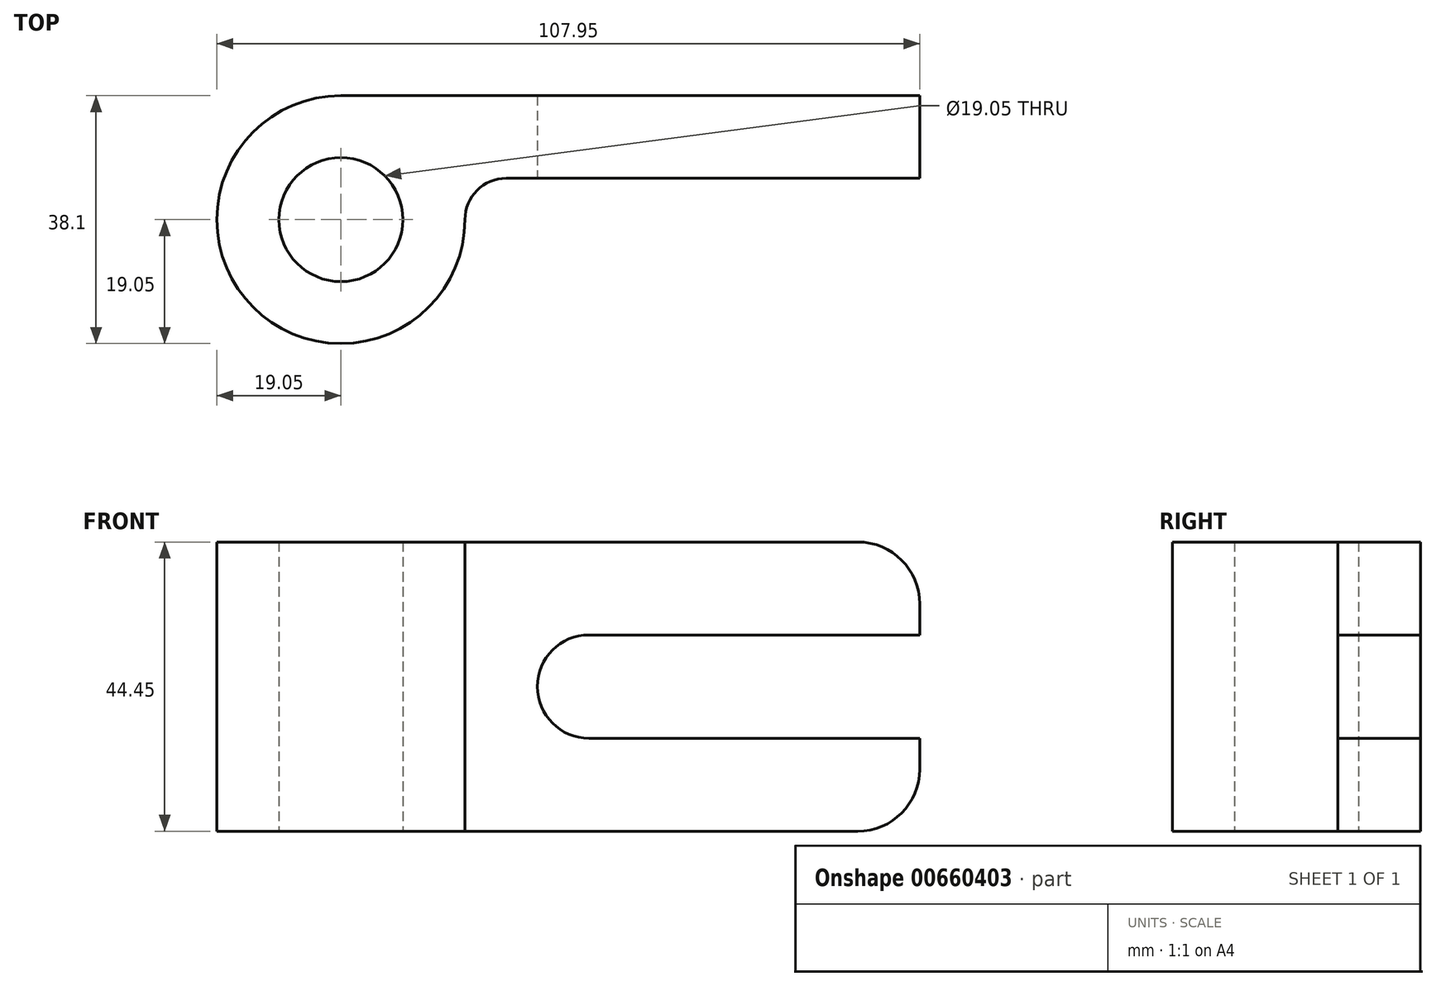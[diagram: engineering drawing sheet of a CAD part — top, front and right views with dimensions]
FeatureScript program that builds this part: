
annotation { "Feature Type Name" : "Feature", "Feature Type Description" : "" }
export const myFeature = defineFeature(function(context is Context, id is Id, definition is map)
    precondition{}
    {
        {
            var Q0;
            Q0=qCreatedBy(makeId("Top.planeOp"),FACE);
            var sketch = newSketch(context, id + "F0", { "sketchPlane" : qUnion([Q0])});
            skArc(sketch, "E0", {"start": v(0, 19.05) * mm, "mid": v(-13.47, -13.47) * mm, "end": v(19.05, 0) * mm});
            skCircle(sketch, "E1", {"center": v(0, 0) * mm, "radius": 9.53 * mm});
            skLineSegment(sketch, "E2", {"start": v(0, 19.05) * mm, "end": v(38.1, 19.05) * mm});
            skLineSegment(sketch, "E3", {"start": v(38.1, 19.05) * mm, "end": v(88.9, 19.05) * mm});
            skLineSegment(sketch, "E4", {"start": v(88.9, 19.05) * mm, "end": v(88.9, 6.35) * mm});
            skLineSegment(sketch, "E5", {"start": v(88.9, 6.35) * mm, "end": v(25.4, 6.35) * mm});
            skArc(sketch, "E6", {"start": v(25.4, 6.35) * mm, "mid": v(20.9, 4.5) * mm, "end": v(19.05, 0) * mm});
            skSolve(sketch);
        }
        {
            var Q0;
            Q0=makeQuery(id+"F0.imprint","IMPRINT",FACE,{"disambiguationData":[TD([[makeQuery(id+"F0.imprint","IMPRINT",EDGE,{"derivedFrom":sQuery(id+"F0.wireOp",EDGE,"E0")}),1.0]])]});
            extrude(context, id + "F1", {"entities" : qUnion([Q0]), "depth" : 44.45 * mm, "offsetDistance" : 25.4 * mm});
        }
        {
            var Q0;
            Q0=makeQuery(id+"F1.opExtrude","SWEPT_FACE",FACE,{"disambiguationData":[OSD([sQuery(id+"F0.wireOp",EDGE,"E5")])]});
            var sketch = newSketch(context, id + "F2", { "sketchPlane" : qUnion([Q0])});
            skArc(sketch, "E7", {"start": v(38.1, 30.16) * mm, "mid": v(30.16, 22.23) * mm, "end": v(38.1, 14.29) * mm});
            skLineSegment(sketch, "E8", {"start": v(38.1, 30.16) * mm, "end": v(88.9, 30.16) * mm});
            skLineSegment(sketch, "E9", {"start": v(38.1, 14.29) * mm, "end": v(88.9, 14.29) * mm});
            skArc(sketch, "E10", {"start": v(71.13, 14.29) * mm, "mid": v(79.38, 0) * mm, "end": v(87.62, 14.29) * mm});
            skArc(sketch, "E11", {"start": v(87.62, 30.16) * mm, "mid": v(79.38, 44.45) * mm, "end": v(71.13, 30.16) * mm});
            skSolve(sketch);
        }
        {
            var Q0;
            {var subQ8=sQuery(id+"F2.wireOp",EDGE,"E7");Q0=makeQuery(id+"F2.imprint","IMPRINT",FACE,{"disambiguationData":[TD([[makeQuery(id+"F2.imprint","IMPRINT",EDGE,{"derivedFrom":subQ8}),1.0]])]});}
            var Q1;
            {var subQ0=sQuery(id+"F2.wireOp",EDGE,"E11");var subQ1=sQuery(id+"F0.wireOp",EDGE,"E5");var subQ4=makeQuery(id+"F1.opExtrude","CAP_EDGE",EDGE,{"disambiguationData":[OSD([subQ1])],"isStart":false});var subQ5=makeQuery(id+"F2.imprint","INTERSECT",VERTEX,{"derivedFrom":[subQ4,subQ0]});Q1=makeQuery(id+"F2.imprint","IMPRINT",FACE,{"disambiguationData":[TD([[makeQuery(id+"F2.imprint","IMPRINT",EDGE,{"disambiguationData":[TD([[subQ5,1.0]])],"derivedFrom":subQ0}),-1.0]])]});}
            var Q2;
            {var subQ0=sQuery(id+"F2.wireOp",EDGE,"E10");var subQ1=sQuery(id+"F0.wireOp",EDGE,"E5");var subQ2=makeQuery(id+"F1.opExtrude","CAP_EDGE",EDGE,{"disambiguationData":[OSD([subQ1])],"isStart":true});var subQ3=makeQuery(id+"F2.imprint","INTERSECT",VERTEX,{"derivedFrom":[subQ2,subQ0]});Q2=makeQuery(id+"F2.imprint","IMPRINT",FACE,{"disambiguationData":[TD([[makeQuery(id+"F2.imprint","IMPRINT",EDGE,{"disambiguationData":[TD([[subQ3,-1.0]])],"derivedFrom":subQ0}),-1.0]])]});}
            extrude(context, id + "F3", {"entities" : qUnion([Q0, Q1, Q2]), "operationType" : NewBodyOperationType.REMOVE, "oppositeDirection" : true, "depth" : 25.4 * mm, "offsetDistance" : 25.4 * mm});
        }
    });
